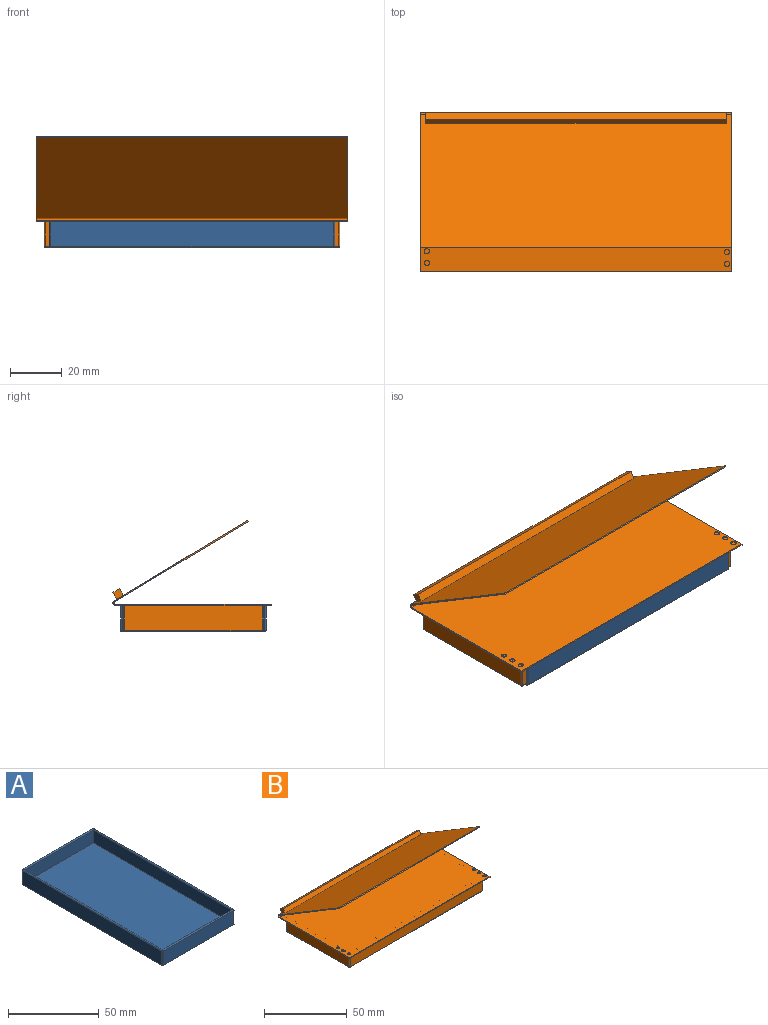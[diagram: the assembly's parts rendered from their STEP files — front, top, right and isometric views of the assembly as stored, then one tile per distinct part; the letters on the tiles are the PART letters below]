
ASSEMBLY  parts=2 mates=1
PART A: 22 faces, bbox 56x110x10 mm
  f0: plane 55x9.5mm, normal (0,1,0), area 522.5mm2, adj f4,f10,f13,f19
  f1: plane 109x9.5mm, normal (-1,0,0), area 1035.5mm2, adj f4,f12,f13,f21
  f2: plane 55x9.5mm, normal (0,-1,0), area 522.5mm2, adj f4,f11,f12,f20
  f3: plane 109x9.5mm, normal (1,0,0), area 1035.5mm2, adj f4,f10,f11,f15
  f4: plane 110x56mm, normal (0,0,-1), area 6159.8mm2, adj f0,f1,f2,f3,f10,f11,f12,f13
  f5: plane 108x8.5mm, normal (-1,0,0), area 918mm2, adj f6,f8,f9,f15
  f6: plane 54x8.5mm, normal (0,-1,0), area 459mm2, adj f5,f7,f9,f19
  f7: plane 108x8.5mm, normal (1,0,0), area 918mm2, adj f6,f8,f9,f21
  f8: plane 54x8.5mm, normal (0,1,0), area 459mm2, adj f5,f7,f9,f20
  f9: plane 108x54mm, normal (0,0,1), area 5832mm2, adj f5,f6,f7,f8
  f10: cylinder r=0.5mm len=9.5mm, axis (0,0,-1), area 7.5mm2, adj f0,f3,f4,f14
  f11: cylinder r=0.5mm len=9.5mm, axis (0,0,1), area 7.5mm2, adj f2,f3,f4,f16
  f12: cylinder r=0.5mm len=9.5mm, axis (0,0,-1), area 7.5mm2, adj f1,f2,f4,f17
  f13: cylinder r=0.5mm len=9.5mm, axis (0,0,1), area 7.5mm2, adj f0,f1,f4,f18
  f14: sphere r=0.5mm, area 0.4mm2, adj f10,f15,f19
  f15: cylinder r=0.5mm len=109mm, axis (0,-1,0), area 170.7mm2, adj f3,f5,f14,f16,f19,f20
  f16: sphere r=0.5mm, area 0.4mm2, adj f11,f15,f20
  f17: sphere r=0.5mm, area 0.4mm2, adj f12,f20,f21
  f18: sphere r=0.5mm, area 0.4mm2, adj f13,f19,f21
  f19: cylinder r=0.5mm len=55mm, axis (1,0,0), area 85.9mm2, adj f0,f6,f14,f15,f18,f21
  f20: cylinder r=0.5mm len=55mm, axis (-1,0,0), area 85.9mm2, adj f2,f8,f15,f16,f17,f21
  f21: cylinder r=0.5mm len=109mm, axis (0,1,0), area 170.7mm2, adj f1,f7,f17,f18,f19,f20
PART B: 48 faces, bbox 120x61.1x42.9 mm
  f0: plane 120x51.36mm, normal (0,0.52,0.86), area 6852mm2, adj f6,f7,f8,f9,f22,f23,f24,f25
  f1: plane 120x51.36mm, normal (0,-0.52,-0.86), area 7200mm2, adj f2,f7,f8,f9
  f2: cylinder r=0.5mm len=120mm, axis (-1,0,0), area 155.9mm2, adj f1,f3,f8,f9
  f3: plane 120x60mm, normal (0,0,1), area 7181.2mm2, adj f2,f4,f8,f9,f10,f12,f14,f16
  f4: plane 120x0.5mm, normal (0,-1,0), area 60mm2, adj f3,f5,f8,f9
  f5: plane 120x60mm, normal (0,0,-1), area 1044.2mm2, adj f4,f6,f8,f9,f27,f28,f29,f34
  f6: cylinder r=1mm len=120mm, axis (-1,0,0), area 311.8mm2, adj f0,f5,f8,f9
  f7: plane 120x0.43mm, normal (0,-0.86,0.52), area 60mm2, adj f0,f1,f8,f9
  f8: plane 61x32.87mm, normal (1,0,0), area 61mm2, adj f0,f1,f2,f3,f4,f5,f6,f7
  f9: plane 61x32.87mm, normal (-1,0,0), area 61mm2, adj f0,f1,f2,f3,f4,f5,f6,f7
  f10: cylinder r=1mm len=2mm, axis (0,0,1), area 1.6mm2, adj f3,f11
  f11: plane 2x2mm, normal (0,0,1), area 3.1mm2, adj f10
  f12: cylinder r=1mm len=2mm, axis (0,0,1), area 1.6mm2, adj f3,f13
  f13: plane 2x2mm, normal (0,0,1), area 3.1mm2, adj f12
  f14: cylinder r=1mm len=2mm, axis (0,0,1), area 1.6mm2, adj f3,f15
  f15: plane 2x2mm, normal (0,0,1), area 3.1mm2, adj f14
  f16: cylinder r=1mm len=2mm, axis (0,0,1), area 1.6mm2, adj f3,f17
  f17: plane 2x2mm, normal (0,0,1), area 3.1mm2, adj f16
  f18: cylinder r=1mm len=2mm, axis (0,0,1), area 1.6mm2, adj f3,f19
  f19: plane 2x2mm, normal (0,0,1), area 3.1mm2, adj f18
  f20: cylinder r=1mm len=2mm, axis (0,0,1), area 1.6mm2, adj f3,f21
  f21: plane 2x2mm, normal (0,0,1), area 3.1mm2, adj f20
  f22: plane 4.12x4.12mm, normal (1,0,0), area 9mm2, adj f0,f23,f25,f26
  f23: plane 116x2.57mm, normal (0,0.86,-0.52), area 348mm2, adj f0,f22,f24,f26
  f24: plane 4.12x4.12mm, normal (-1,0,0), area 9mm2, adj f0,f23,f25,f26
  f25: plane 116x2.57mm, normal (0,-0.86,0.52), area 348mm2, adj f0,f22,f24,f26
  f26: plane 116x2.57mm, normal (0,0.52,0.86), area 348mm2, adj f22,f23,f24,f25
  f27: plane 113x9.5mm, normal (0,1,0), area 1073.5mm2, adj f5,f38,f43,f47
  f28: plane 53x9.5mm, normal (1,0,0), area 503.5mm2, adj f5,f41,f44,f47
  f29: plane 113x9.5mm, normal (0,-1,0), area 1073.5mm2, adj f5,f36,f40,f41
  f30: plane 52x9.5mm, normal (-1,0,0), area 494mm2, adj f31,f33,f35,f44
  f31: plane 112x9.5mm, normal (0,-1,0), area 1064mm2, adj f30,f32,f35,f43
  f32: plane 52x9.5mm, normal (1,0,0), area 494mm2, adj f31,f33,f35,f39
  f33: plane 112x9.5mm, normal (0,1,0), area 1064mm2, adj f30,f32,f35,f40
  f34: plane 53x9.5mm, normal (-1,0,0), area 503.5mm2, adj f5,f36,f38,f39
  f35: plane 112x52mm, normal (0,0,-1), area 5824mm2, adj f30,f31,f32,f33
  f36: cylinder r=0.5mm len=9.5mm, axis (0,0,1), area 7.5mm2, adj f5,f29,f34,f37
  f37: sphere r=0.5mm, area 0.4mm2, adj f36,f39,f40
  f38: cylinder r=0.5mm len=9.5mm, axis (0,0,-1), area 7.5mm2, adj f5,f27,f34,f42
  f39: cylinder r=0.5mm len=53mm, axis (0,-1,0), area 82.8mm2, adj f32,f34,f37,f40,f42,f43
  f40: cylinder r=0.5mm len=113mm, axis (-1,0,0), area 177mm2, adj f29,f33,f37,f39,f44,f45
  f41: cylinder r=0.5mm len=9.5mm, axis (0,0,-1), area 7.5mm2, adj f5,f28,f29,f45
  f42: sphere r=0.5mm, area 0.4mm2, adj f38,f39,f43
  f43: cylinder r=0.5mm len=113mm, axis (1,0,0), area 177mm2, adj f27,f31,f39,f42,f44,f46
  f44: cylinder r=0.5mm len=53mm, axis (0,-1,0), area 82.8mm2, adj f28,f30,f40,f43,f45,f46
  f45: sphere r=0.5mm, area 0.4mm2, adj f40,f41,f44
  f46: sphere r=0.5mm, area 0.4mm2, adj f43,f44,f47
  f47: cylinder r=0.5mm len=9.5mm, axis (0,0,1), area 7.5mm2, adj f5,f27,f28,f46
PLACE A rot(axis=(-0.71,-0.71,0),180deg) t=(37.52,1.86,4)mm
PLACE B t=(37.52,-28.14,4.5)mm
MATE planar B.f35 <-> A.f4  axis (0,0,-1) through (37.52,1.86,4)mm
